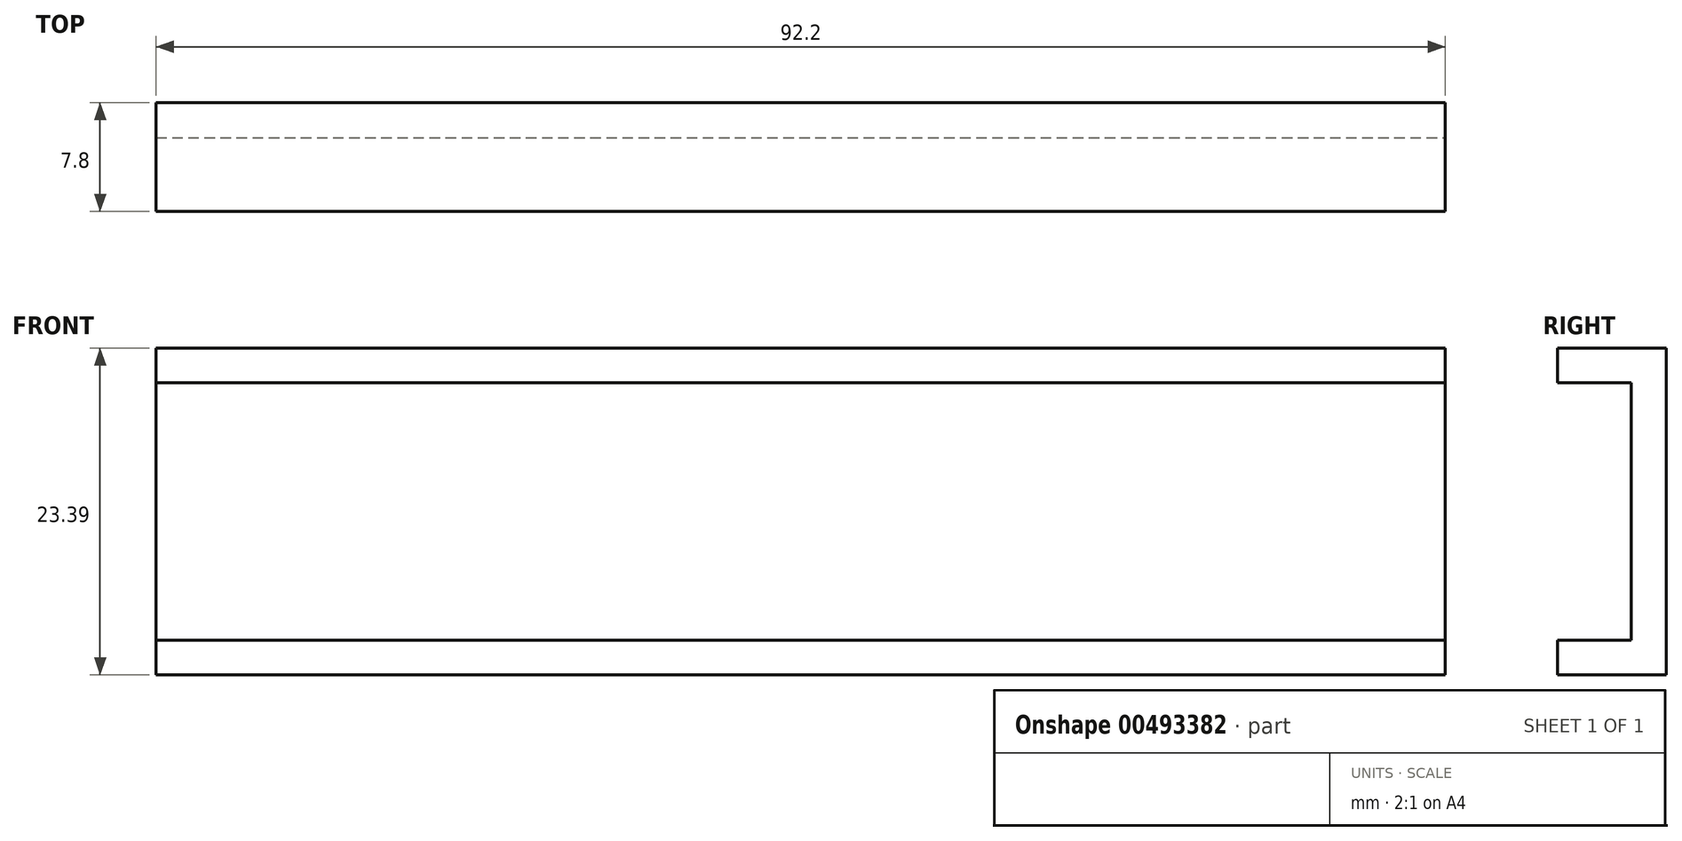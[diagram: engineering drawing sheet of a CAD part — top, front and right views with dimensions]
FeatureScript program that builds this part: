
annotation { "Feature Type Name" : "Feature", "Feature Type Description" : "" }
export const myFeature = defineFeature(function(context is Context, id is Id, definition is map)
    precondition{}
    {
        {
            var Q0;
            Q0=qCreatedBy(makeId("Front.planeOp"),FACE);
            var sketch = newSketch(context, id + "F0", { "sketchPlane" : qUnion([Q0])});
            skLineSegment(sketch, "E0.bottom", {"start": v(-56.27, -8.85) * mm, "end": v(60.93, -8.85) * mm});
            skLineSegment(sketch, "E0.top", {"start": v(-56.27, -32.24) * mm, "end": v(60.93, -32.24) * mm});
            skLineSegment(sketch, "E0.left", {"start": v(-56.27, -8.85) * mm, "end": v(-56.27, -32.24) * mm});
            skLineSegment(sketch, "E0.right", {"start": v(60.93, -8.85) * mm, "end": v(60.93, -32.24) * mm});
            skSolve(sketch);
        }
        {
            var Q0;
            Q0=makeQuery(id+"F0.imprint","IMPRINT",FACE,{"disambiguationData":[TD([[makeQuery(id+"F0.imprint","IMPRINT",EDGE,{"derivedFrom":sQuery(id+"F0.wireOp",EDGE,"E0.bottom")}),-1.0]])]});
            extrude(context, id + "F1", {"entities" : qUnion([Q0]), "endBound" : BoundingType.SYMMETRIC, "depth" : 7.8 * mm});
        }
        {
            var Q0;
            Q0=makeQuery(id+"F1.opExtrude","CAP_FACE",FACE,{"disambiguationData":[OSD([sQuery(id+"F0.wireOp",EDGE,"E0.bottom"),sQuery(id+"F0.wireOp",EDGE,"E0.top"),sQuery(id+"F0.wireOp",EDGE,"E0.left"),sQuery(id+"F0.wireOp",EDGE,"E0.right")])],"isStart":false});
            shell(context, id + "F2", {"entities" : qUnion([Q0]), "thickness" : 2.5 * mm});
        }
        {
            var Q0;
            Q0=makeQuery(id+"F1.opExtrude","SWEPT_FACE",FACE,{"disambiguationData":[OSD([sQuery(id+"F0.wireOp",EDGE,"E0.right")])]});
            extrude(context, id + "F3", {"entities" : qUnion([Q0]), "operationType" : NewBodyOperationType.REMOVE, "endBound" : BoundingType.SYMMETRIC, "oppositeDirection" : true, "depth" : 25 * mm});
        }
        {
            var Q0;
            Q0=makeQuery(id+"F1.opExtrude","SWEPT_FACE",FACE,{"disambiguationData":[OSD([sQuery(id+"F0.wireOp",EDGE,"E0.left")])]});
            extrude(context, id + "F4", {"entities" : qUnion([Q0]), "operationType" : NewBodyOperationType.REMOVE, "endBound" : BoundingType.SYMMETRIC, "oppositeDirection" : true, "depth" : 25 * mm});
        }
    });
